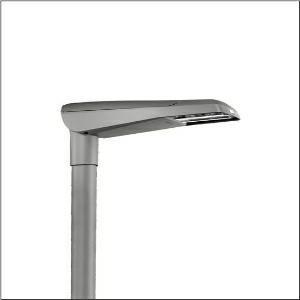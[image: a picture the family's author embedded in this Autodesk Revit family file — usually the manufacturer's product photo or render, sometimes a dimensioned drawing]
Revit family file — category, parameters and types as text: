
# Revit family: streetlight_sl_11_iq_micro___st1_2a_5xc1ac1g08de_fbfe
name_source: partatom
category: Lighting Fixtures
units: mm (PartAtom-declared; Revit-internal decimal feet)

## family parameters
Cut with Voids When Loaded = No
Host = Face
Light Source = No
Part Type = Normal
Room Calculation Point = No
Round Connector Dimension = Use Diameter
Shared = No

## types (1)
- --- (1 x LED, 3860 lm, 27.4 W, 4000K)
    Apparent Load = 27 VA
    CIE Flux Codes = 33 71 96 100 100
    Color Rendering = 70
    Color Temperature = 4000K
    Default Elevation = 1800 mm
    Description = Streetlight SL 11 iQ micro, mast luminaire, primary light control with 3 zone facetted reflector, of plastic, silver coated, highly specular, primary optical cover: cover, of PMMA, transparent, light distribution: ST1.2a, light emission: direct distribution, primary light characteristic: asymmetric, installation type: post-top, side-entry, lamps: LED, High Power LED, rated values: 3.620lm | 27,7W | 130,7lm/W (begin service life); end service life: 3.620lm | 28,1W; at 50% lumin. flux: 1.810lm | 13,4W | 135,1lm/W, colour temperature: 2200/2700/3000/4000K, colour rendering: CRI > 70, light colour: 722/727/730/740, light setting 1 begin service life: 100% | 3.620lm | 27,7W | 130,7lm/W | 3.000K, light setting 1 end service life: 28,1W, further light settings possible, control: pre-setting: linear dimming characteristic, Street-Remote, Auto-Match, Temp-Guard, Lumen-Switch, Night-Set, Smart-Wire, Light-Fading, Desk-Remote (wireless, voltage-free reading and setting of iQ features in the workshop via application-optimized NFC function/RFID function), optimised constant luminous flux control (CLO 2.0), with cable H07RN-F 5x 1.5mm², mains connection: 220..240V, AC, 50/60Hz, connection cable pre-assembled, cable length: 6,5m, luminaire housing, of diecast aluminium, powder-coated, Siteco® metallic grey (DB 702S), please order mast flange separately, inclination adjustable without tools: 0°, 5°, 10°, 15° (post-top) | 0°, -5°, -10°, -15° (side-entry), sealing non-destructively replaceable, multi-level sealing system, length: 600mm, width: 174mm, height: 116mm, mast flange for spigot size: 42mm (side-entry): 5XC10008XM4, 60/48mm (side-entry/post-top): 5XC10108XM2, 76/60mm (side-entry/post-top): 5XC10108XM1, equipment: Power, protection rating (complete): IP66, insulation class (complete): insulation class II (safety insulation), certification: CE, ENEC, ENEC+, VDE, impact resistance: IK10, permissible operating ambient temperature for outdoor applications: -25..+50°C, standard-compliant lighting for roads and squares, Environmental Product Declaration (EPD) tested and certified by an independent institute, packaging unit: 1 piece

Light Distribution: ST1.2a
    Height = 116 mm
    Lamp = 1 x LED
    Lamp Light Flux = 3860 lm
    Lamp Power = 27.4 W
    Lamp count = 1
    Length = 600 mm
    Luminous efficacy = 141 lm/W
    Manufacturer = Siteco
    ModVariant = No
    Model = 5XC1AC1G08DE
    Number of Poles = 1
    OnlyDefault = Yes
    Power Factor = 1
    Product Name = Streetlight SL 11 iQ micro | ST1.2a
    Product group = mast luminaire | pylon top
    ProductGroupID = 6100
    Protection Class = Protection class II
    Protection Degree = IP 66
    RLX_Detail_Level = 1
    RLX_Emergency_Light_Flux = 0 lm
    RLX_Emergency_Type = 0
    RLX_Emergency_Type_DB = No
    RlxData = <blob elided: 59661 chars, md5=17b14129>
    Socket = socket
    Standby Power = 0 W
    System Light Flux = 3860 lm
    System Power = 27 W
    Type Comments = individual setting: luminous flux: 100 % | dim-lin: 254 | 726 mA
    Type Image = l_1006566.jpg
    URL = http://relux.com
    VarID = @adj_040356
    Voltage = 0 V
    Weight = 0.00 kg
    Width = 174 mm

## geometry (parser evidence)
native form markers: Blend x4, Sweep x13
no freeform markers — native parametric forms only
